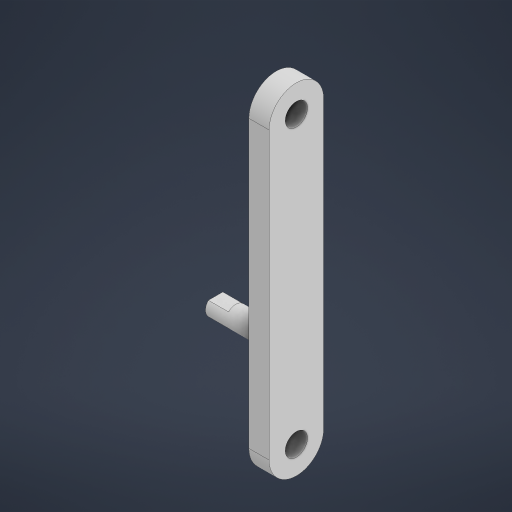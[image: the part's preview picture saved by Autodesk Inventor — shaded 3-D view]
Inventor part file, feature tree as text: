
AUTODESK INVENTOR PART (.ipt)
format: ipt  version: 2024 (Build 280153000, 153)  size: 194,560 bytes
history: native  units: mm
features: extrude x3, sketch x1
ambient origin geometry x8: Origin, YZ Plane, XZ Plane, XY Plane, X Axis, Y Axis, Z Axis, Center Point
bodies: Body1 (feature_tree)
feature tree (4):
  sketch  "스케치4"
  extrude  "돌출6"  Depth=5.5mm
  extrude  "돌출7"  Depth=13.5mm
  extrude  "돌출8"  Depth=70.8mm
